# Revit family: Window_Curtain_Wall-Single_Hung-Traco-TR_9100-Heavy_Commercial-Tri_Lite
name_source: partatom
category: Windows
revit_build: Autodesk Revit 2015 (Build: 20140905_0730(x64)
units: mm (PartAtom-declared; Revit-internal decimal feet)

## types (1)
- TR-9100 - SH/Fixed-Bottom
    Allowable Air Infiltration Maximum = 0.3 @ 6.2 PSF
    Assembly Code = B2020110
    CTRL Panel Trim Depth = 0' - 0 3/4"
    CTRL Panel Trim Height = 0' - 1 1/4"
    Condensation Resistance = 0.0000 psf
    Depth = 0' - 3 1/4"
    Description = Heavy Commercial, Single Hung, Side Load
    Designation = AAMA/WDMA/CSA 101/I.S.2/A-440-05: H-AW50 And AAMA/WDMA/CSA 101/I.S.2/A-440-08: AW-PG50-H
    Forced Entry Resistance = TYPE A: GRADE 10
    Frame Material = Aluminum - Traco - Anodized - Gray
    Glazing Material = Glass - Traco - Clear
    Glazing Thickness = 0' - 1"
    Has Muntins = No
    Head Width = 0' - 1"
    Height Maximum = 10' - 0"
    Height Minimum = 2' - 0"
    Keynote = 08500
    Manufacturer = Traco
    Model = TR-9100 Tri-Lite
    Panel Material = <By Category>
    Panel Thickness = 0' - 2"
    Product Documentation Link = http://www.alcoa.com
    Product Page URL = http://www.alcoa.com
    Product data url = https://bimobject.com
    Rail Width = 0' - 2"
    Sill Width = 0' - 1"
    Test Size = 60" X 99"
    Type Comments = Single Hung with Bottom Panel
    U Factor = .45 Per NFRC 100
    URL = http://www.alcoa.com
    Uniform Load Deflection = 50.0000 psf
    Uniform Load Structural = 75.0000 psf
    Water Resistance = 15.0000 psf
    Width Maximum = 10' - 0"
    Width Minimum = 2' - 0"

## geometry (parser evidence)
native form markers: Blend x6, Sweep x12
no freeform markers — native parametric forms only
